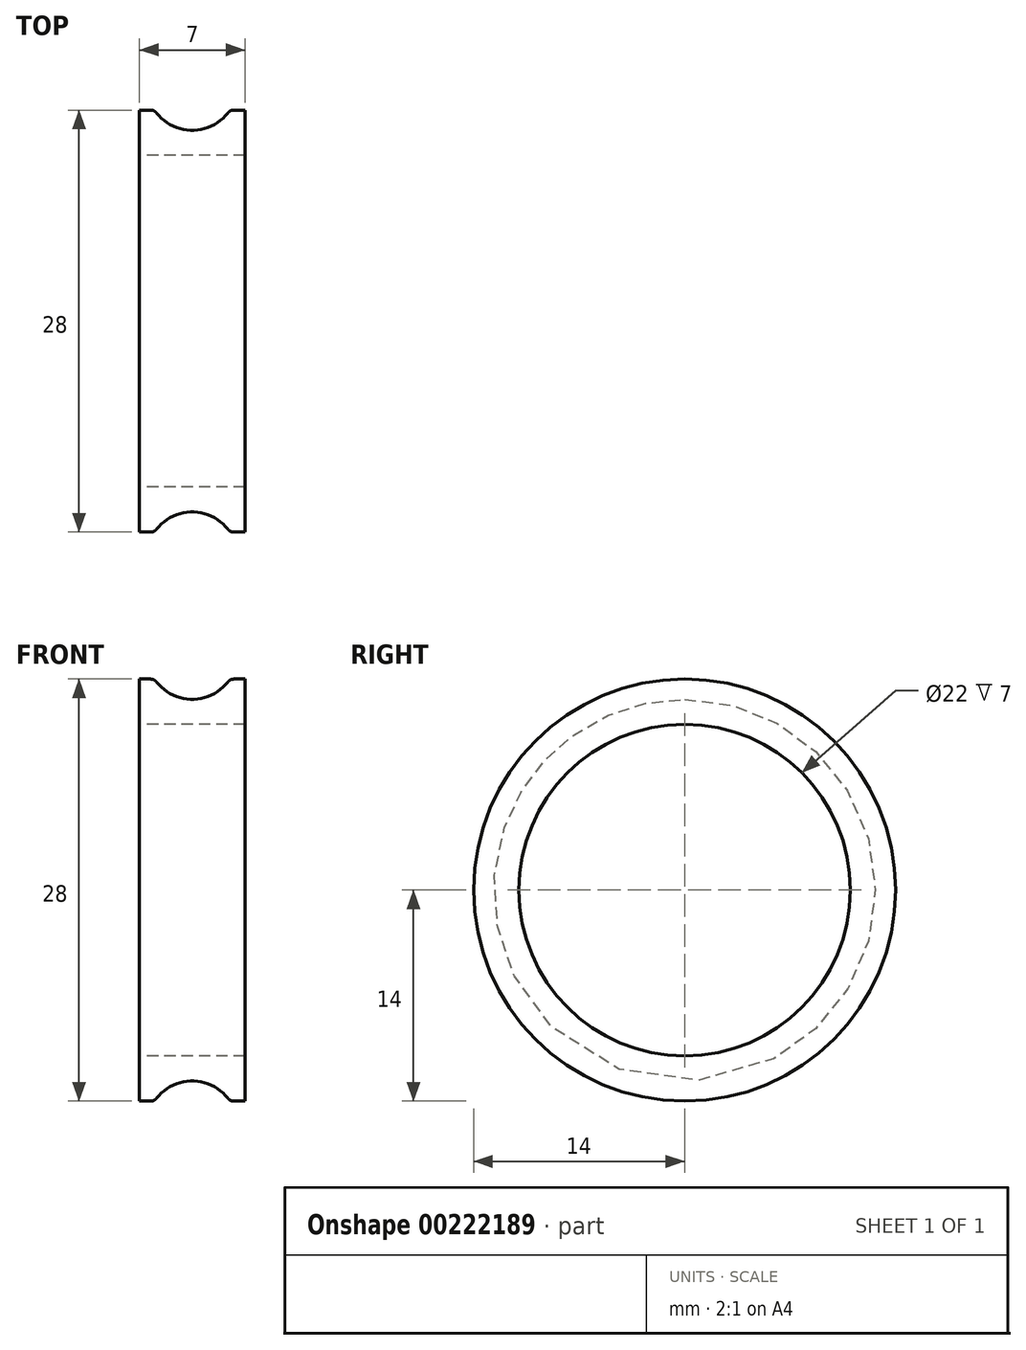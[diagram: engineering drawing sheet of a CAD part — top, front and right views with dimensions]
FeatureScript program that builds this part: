
annotation { "Feature Type Name" : "Feature", "Feature Type Description" : "" }
export const myFeature = defineFeature(function(context is Context, id is Id, definition is map)
    precondition{}
    {
        {
            var Q0;
            Q0=qCreatedBy(makeId("Top.planeOp"),FACE);
            var sketch = newSketch(context, id + "F0", { "sketchPlane" : qUnion([Q0])});
            skLineSegment(sketch, "E0.bottom", {"start": v(3.5, -1.5) * mm, "end": v(-3.5, -1.5) * mm});
            skLineSegment(sketch, "E0.top", {"start": v(3.5, 1.5) * mm, "end": v(-3.5, 1.5) * mm});
            skLineSegment(sketch, "E0.left", {"start": v(3.5, -1.5) * mm, "end": v(3.5, 1.5) * mm});
            skLineSegment(sketch, "E0.right", {"start": v(-3.5, -1.5) * mm, "end": v(-3.5, 1.5) * mm});
            skPoint(sketch, "E0.middle", {"position": v(0, 0) * mm});
            skArc(sketch, "E1", {"start": v(-2.5, 1.5) * mm, "mid": v(0, 0.16) * mm, "end": v(2.5, 1.5) * mm});
            skLineSegment(sketch, "E2.bottom", {"start": v(-3.5, -1.5) * mm, "end": v(3.5, -1.5) * mm, "construction": true});
            skLineSegment(sketch, "E2.top", {"start": v(-3.5, -12.5) * mm, "end": v(3.5, -12.5) * mm, "construction": true});
            skLineSegment(sketch, "E2.left", {"start": v(-3.5, -1.5) * mm, "end": v(-3.5, -12.5) * mm, "construction": true});
            skLineSegment(sketch, "E2.right", {"start": v(3.5, -1.5) * mm, "end": v(3.5, -12.5) * mm, "construction": true});
            skSolve(sketch);
        }
        {
            var Q0;
            Q0=makeQuery(id+"F0.imprint","IMPRINT",FACE,{"disambiguationData":[TD([[makeQuery(id+"F0.imprint","IMPRINT",EDGE,{"derivedFrom":sQuery(id+"F0.wireOp",EDGE,"E0.bottom")}),-1.0]])]});
            var Q1;
            Q1=sQuery(id+"F0.wireOp",EDGE,"E2.top");
            revolve(context, id + "F1", {"entities" : qUnion([Q0]), "axis" : qUnion([Q1]), "revolveType" : RevolveType.FULL});
        }
        {
            var Q0;
            {var subQ0=sQuery(id+"F0.wireOp",EDGE,"E1");var subQ1=sQuery(id+"F0.wireOp",EDGE,"E0.top");Q0=makeQuery(id+"F1.opRevolve","SWEPT_EDGE",EDGE,{"disambiguationData":[OSD([subQ1,subQ0]),TDD([makeQuery(id+"F0.imprint","INTERSECT",VERTEX,{"disambiguationData":[OD(1.0)],"derivedFrom":[subQ1,subQ0]})])]});}
            var Q1;
            {var subQ0=sQuery(id+"F0.wireOp",EDGE,"E1");var subQ1=sQuery(id+"F0.wireOp",EDGE,"E0.top");Q1=makeQuery(id+"F1.opRevolve","SWEPT_EDGE",EDGE,{"disambiguationData":[OSD([subQ1,subQ0]),TDD([makeQuery(id+"F0.imprint","INTERSECT",VERTEX,{"disambiguationData":[OD(0.0)],"derivedFrom":[subQ1,subQ0]})])]});}
            fillet(context, id + "F2", {"entities" : qUnion([Q0, Q1]), "radius" : 0.5 * mm, "tangentPropagation" : true, "allowEdgeOverflow" : false});
        }
    });
